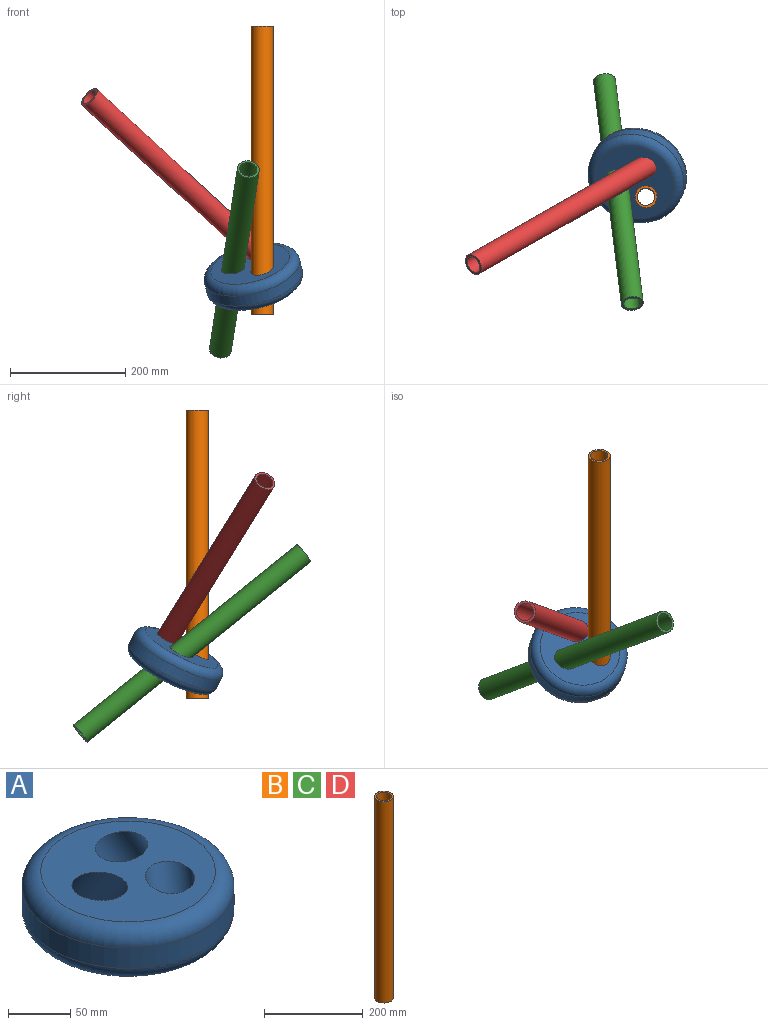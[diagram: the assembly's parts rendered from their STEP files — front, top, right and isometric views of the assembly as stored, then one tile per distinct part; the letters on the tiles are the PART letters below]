
ASSEMBLY  parts=4 mates=3
PART A: 8 faces, bbox 188.4x188.4x93.1 mm
  f0: cylinder r=85mm len=170mm, axis (0,0,-1), area 10681.4mm2, adj f6,f7
  f1: plane 144.41x144.41mm, normal (0,0,1), area 11255.6mm2, adj f3,f4,f5,f7
  f2: plane 140x138.72mm, normal (0,0,-1), area 11685.7mm2, adj f3,f4,f5,f6
  f3: cylinder r=19.5mm len=87.28mm, axis (0.5,0,-0.87), area 6979.4mm2, adj f1,f2,f6
  f4: cylinder r=19.5mm len=88.32mm, axis (-0.25,-0.43,-0.87), area 7025.2mm2, adj f1,f2,f6
  f5: cylinder r=19.5mm len=88.66mm, axis (-0.25,0.43,-0.87), area 7050.7mm2, adj f1,f2,f6
  f6: torus R=70mm, axis (0,0,1), area 11373.1mm2, adj f0,f2,f3,f4,f5
  f7: torus R=70mm, axis (0,0,1), area 11776.8mm2, adj f0,f1
PART B: 4 faces, bbox 38x38x500 mm
  f0: cylinder r=15mm len=500mm, axis (0,0,-1), area 47123.9mm2, adj f2,f3
  f1: cylinder r=19mm len=500mm, axis (0,0,-1), area 59690.3mm2, adj f2,f3
  f2: plane 38x38mm, normal (0,0,1), area 427.3mm2, adj f0,f1
  f3: plane 38x38mm, normal (0,0,-1), area 427.3mm2, adj f0,f1
PART C: same geometry as B
PART D: same geometry as B
PLACE A rot(axis=(0.88,-0.47,0.11),30.2deg) t=(-99.41,171.12,-224.29)mm
PLACE B rot(axis=(0,0,1),0deg) t=(-86.89,133.55,-290.27)mm
PLACE C rot(axis=(0.97,0,0.25),53.1deg) t=(-159.16,336.08,-351.33)mm
PLACE D rot(axis=(0.52,-0.85,-0.07),51.5deg) t=(-47.58,209.68,-225.9)mm
MATE slider A.f4 <-> B.f1  axis (0,0,-1) through (-86.89,133.55,-240.27)mm
MATE slider A.f3 <-> D.f1  axis (0.68,0.39,-0.62) through (-98.76,180.43,-178.7)mm
MATE slider A.f5 <-> C.f0  axis (-0.1,0.77,-0.63) through (-149.79,261.05,-290.79)mm
